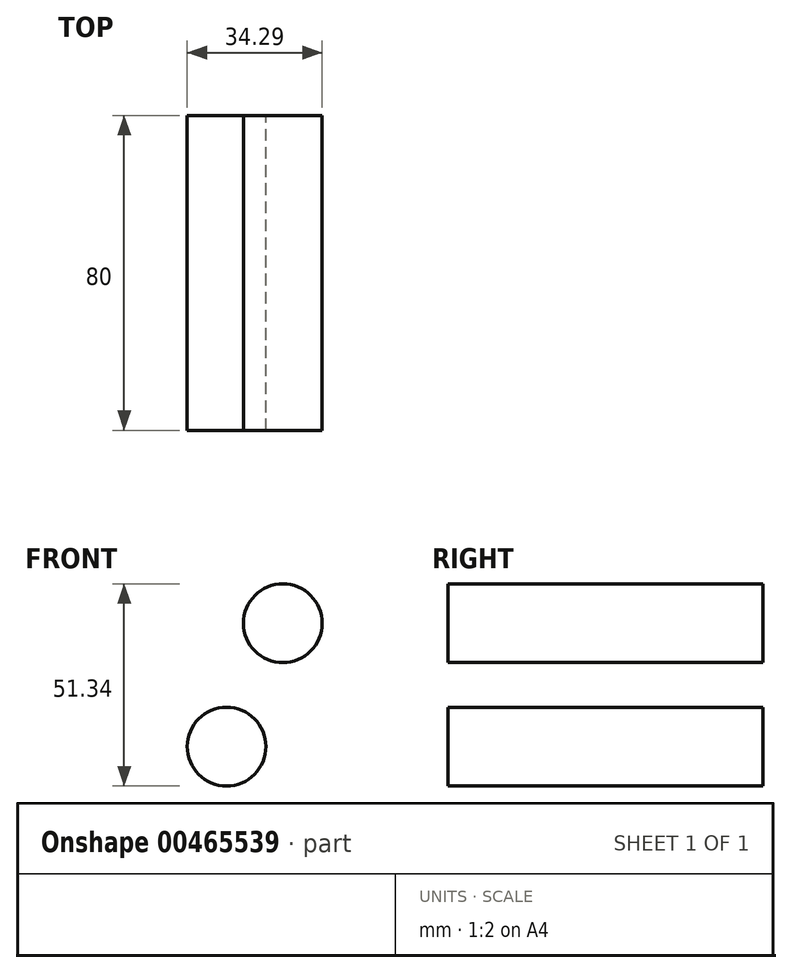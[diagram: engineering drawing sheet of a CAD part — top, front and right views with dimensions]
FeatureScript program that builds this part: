
annotation { "Feature Type Name" : "Feature", "Feature Type Description" : "" }
export const myFeature = defineFeature(function(context is Context, id is Id, definition is map)
    precondition{}
    {
        {
            var Q0;
            Q0=qCreatedBy(makeId("Front.planeOp"),FACE);
            var sketch = newSketch(context, id + "F0", { "sketchPlane" : qUnion([Q0])});
            skCircle(sketch, "E0", {"center": v(-6.96, 25.6) * mm, "radius": 10 * mm});
            skCircle(sketch, "E1", {"center": v(-21.25, -5.74) * mm, "radius": 10 * mm});
            skSolve(sketch);
        }
        {
            var Q0;
            Q0=makeQuery(id+"F0.imprint","IMPRINT",FACE,{"disambiguationData":[TD([[makeQuery(id+"F0.imprint","IMPRINT",EDGE,{"derivedFrom":sQuery(id+"F0.wireOp",EDGE,"E0")}),1.0]])]});
            var Q1;
            Q1=makeQuery(id+"F0.imprint","IMPRINT",FACE,{"disambiguationData":[TD([[makeQuery(id+"F0.imprint","IMPRINT",EDGE,{"derivedFrom":sQuery(id+"F0.wireOp",EDGE,"E1")}),1.0]])]});
            extrude(context, id + "F1", {"entities" : qUnion([Q0, Q1]), "depth" : 80 * mm});
        }
    });
